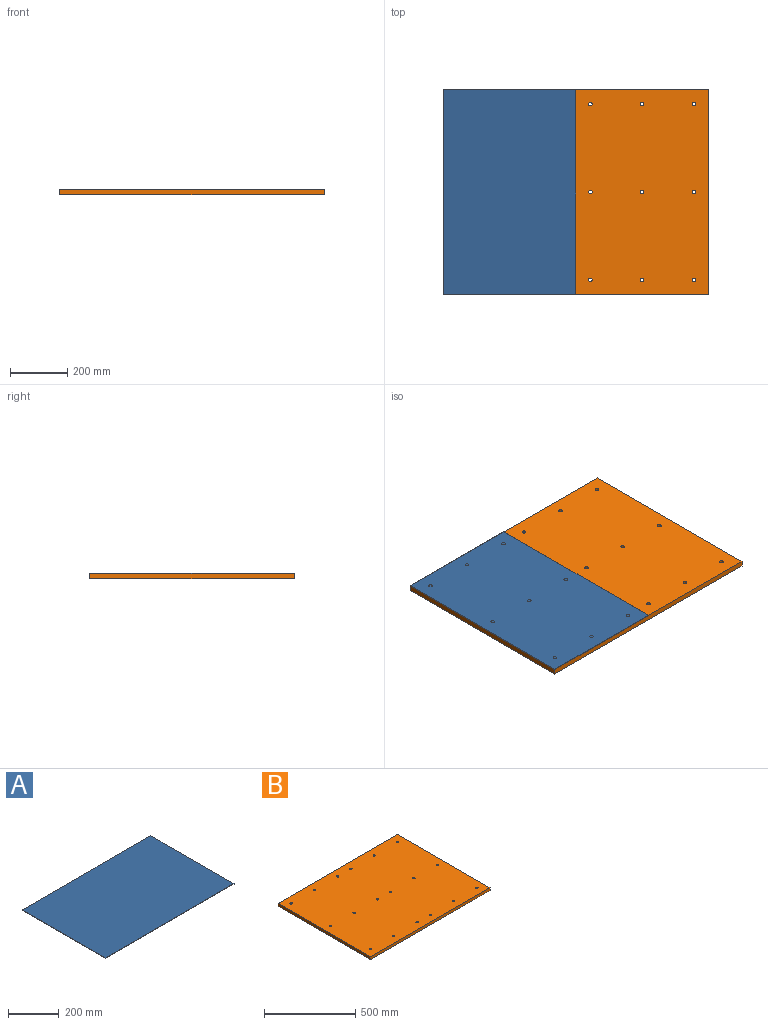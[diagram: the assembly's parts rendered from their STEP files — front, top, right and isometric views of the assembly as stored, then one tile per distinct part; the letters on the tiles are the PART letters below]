
ASSEMBLY  parts=2 mates=1
PART A: 6 faces, bbox 717.6x463.6x1.6 mm
  f0: plane 717.55x1.59mm, normal (0,-1,0), area 1139.1mm2, adj f1,f3,f4,f5
  f1: plane 463.55x1.59mm, normal (1,0,0), area 735.9mm2, adj f0,f2,f4,f5
  f2: plane 717.55x1.59mm, normal (0,1,0), area 1139.1mm2, adj f1,f3,f4,f5
  f3: plane 463.55x1.59mm, normal (-1,0,0), area 735.9mm2, adj f0,f2,f4,f5
  f4: plane 717.55x463.55mm, normal (0,0,1), area 332620.3mm2, adj f0,f1,f2,f3
  f5: plane 717.55x463.55mm, normal (0,0,-1), area 332620.3mm2, adj f0,f1,f2,f3
PART B: 24 faces, bbox 927.1x717.6x19.1 mm
  f0: plane 927.1x717.55mm, normal (0,0,1), area 662960.4mm2, adj f2,f3,f4,f5,f6,f7,f8,f9
  f1: plane 927.1x717.55mm, normal (0,0,-1), area 662960.4mm2, adj f2,f3,f4,f5,f6,f7,f8,f9
  f2: plane 927.1x19.05mm, normal (0,-1,0), area 17661.3mm2, adj f0,f1,f3,f5
  f3: plane 717.55x19.05mm, normal (1,0,0), area 13669.3mm2, adj f0,f1,f2,f4
  f4: plane 927.1x19.05mm, normal (0,1,0), area 17661.3mm2, adj f0,f1,f3,f5
  f5: plane 717.55x19.05mm, normal (-1,0,0), area 13669.3mm2, adj f0,f1,f2,f4
  f6: cylinder r=6.35mm len=19.05mm, axis (0,0,1), area 760.1mm2, adj f0,f1
  f7: cylinder r=6.35mm len=19.05mm, axis (0,0,1), area 760.1mm2, adj f0,f1
  f8: cylinder r=6.35mm len=19.05mm, axis (0,0,1), area 760.1mm2, adj f0,f1
  f9: cylinder r=6.35mm len=19.05mm, axis (0,0,1), area 760.1mm2, adj f0,f1
  f10: cylinder r=6.35mm len=19.05mm, axis (0,0,1), area 760.1mm2, adj f0,f1
  f11: cylinder r=6.35mm len=19.05mm, axis (0,0,1), area 760.1mm2, adj f0,f1
  f12: cylinder r=6.35mm len=19.05mm, axis (0,0,1), area 760.1mm2, adj f0,f1
  f13: cylinder r=6.35mm len=19.05mm, axis (0,0,1), area 760.1mm2, adj f0,f1
  f14: cylinder r=6.35mm len=19.05mm, axis (0,0,1), area 760.1mm2, adj f0,f1
  f15: cylinder r=6.35mm len=19.05mm, axis (0,0,1), area 760.1mm2, adj f0,f1
  f16: cylinder r=6.35mm len=19.05mm, axis (0,0,1), area 760.1mm2, adj f0,f1
  f17: cylinder r=6.35mm len=19.05mm, axis (0,0,1), area 760.1mm2, adj f0,f1
  f18: cylinder r=6.35mm len=19.05mm, axis (0,0,1), area 760.1mm2, adj f0,f1
  f19: cylinder r=6.35mm len=19.05mm, axis (0,0,1), area 760.1mm2, adj f0,f1
  f20: cylinder r=6.35mm len=19.05mm, axis (0,0,1), area 760.1mm2, adj f0,f1
  f21: cylinder r=6.35mm len=19.05mm, axis (0,0,1), area 760.1mm2, adj f0,f1
  f22: cylinder r=6.35mm len=19.05mm, axis (0,0,1), area 760.1mm2, adj f0,f1
  f23: cylinder r=6.35mm len=19.05mm, axis (0,0,1), area 760.1mm2, adj f0,f1
PLACE A rot(axis=(0,0,1),90deg) t=(-231.78,0,19.05)mm
PLACE B at identity
MATE fastened B.f0 <-> A.f5  axis (0,0,1) through (-463.55,-358.78,19.05)mm
